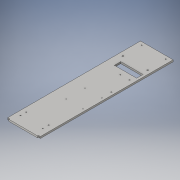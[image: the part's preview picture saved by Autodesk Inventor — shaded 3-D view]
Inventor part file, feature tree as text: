
AUTODESK INVENTOR PART (.ipt)
format: ipt  version: 2016 (Build 200138000, 138)  size: 254,464 bytes
history: native  units: in
note: dims shown in document units (in); Inventor stores cm internally (conversion verified against a paired STEP export)
features: extrude x11, sketch x11
ambient origin geometry x8: Origin, YZ Plane, XZ Plane, XY Plane, X Axis, Y Axis, Z Axis, Center Point
bodies: Solid1 (feature_tree)
feature tree (22):
  extrude  "Extrusion1"  Depth=3.94in
  extrude  "Extrusion3"  Depth=0.213in
  extrude  "Extrusion4"  Depth=2.9in
  extrude  "Extrusion5"  Depth=1.0in TaperAngle=0.0deg
  extrude  "Extrusion6"  Depth=0.25in
  extrude  "Extrusion7"  Depth=0.25in TaperAngle=0.0deg
  extrude  "Extrusion8"  Depth=0.1181in
  extrude  "Extrusion9"  Depth=2.147in TaperAngle=0.0deg
  extrude  "Extrusion10"  Depth=3.0in
  extrude  "Extrusion11"  Depth=0.477in
  extrude  "Extrusion12"  Depth=0.935in
  sketch  "Sketch1"  dims[d0=3.94in d1=14.0in]
  sketch  "Sketch5"  dims[d2=0.213in d3=0.0in d8=0.1181in]
  sketch  "Sketch6"  dims[d9=0.1181in d10=2.9in]
  sketch  "Sketch7"  dims[d11=0.379in d12=1.0in d13=0.0in]
  sketch  "Sketch8"  dims[d14=0.11in d15=0.25in]
  sketch  "Sketch9"  dims[d16=0.25in d17=1.0in d18=0.0in]
  sketch  "Sketch10"  dims[d19=0.1181in d20=0.1181in]
  sketch  "Sketch11"  dims[d21=10.0in d22=0.0in d23=2.147in d24=0.0in]
  sketch  "Sketch12"  dims[d25=2.147in d26=0.0in d27=3.0in]
  sketch  "Sketch13"  dims[d28=1.0in d29=0.477in]
  sketch  "Sketch14"  dims[d30=0.463in d31=0.935in d32=0.3in d33=0.3in d34=1.0in d35=1.0in d36=2.7in d37=0.7in d38=0.7in d39=2.7in d40=0.1181in d41=0.1181in d42=0.1181in d43=0.1181in d44=0.15in d45=1.0in d46=1.0in d47=0.3in d48=0.3in d49=0.3in d50=0.3in d51=3.0in d52=1.0in d53=1.0in d54=0.7in d55=2.147in d56=0.0in d57=5.579in d58=0.323in d59=0.086in d60=0.086in d62=2.036in d63=2.281in d64=2.281in d65=2.147in d66=0.0in d67=0.121in d68=0.341in d69=8.925in d75=1.0in d76=0.0in d89=0.599in d90=0.104in d91=2.958in d92=2.103in d93=0.08in d94=0.116in d95=1.472in d96=0.55in d97=2.958in d98=0.121in d99=0.104in d100=0.121in d101=0.104in d102=1.098in d103=0.297in d104=2.3788in d105=1.0in d106=0.0in d107=3.3244in d108=0.429in d109=0.5in d110=0.084in d111=0.084in d114=0.274in d115=1.0in d116=0.0in]
